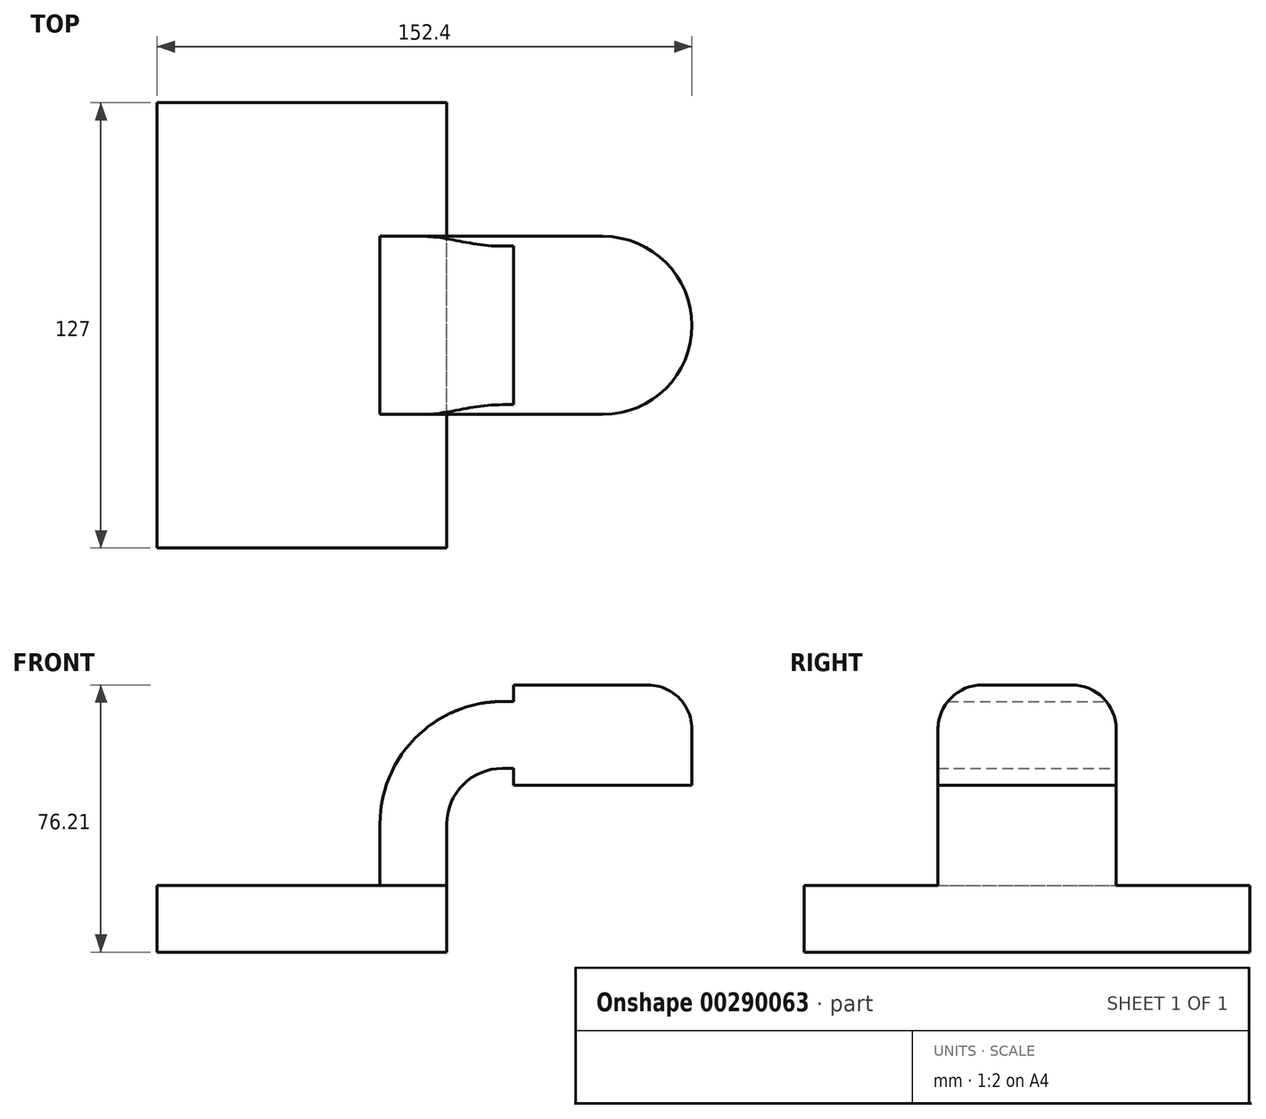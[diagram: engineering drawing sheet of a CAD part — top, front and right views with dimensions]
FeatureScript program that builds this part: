
annotation { "Feature Type Name" : "Feature", "Feature Type Description" : "" }
export const myFeature = defineFeature(function(context is Context, id is Id, definition is map)
    precondition{}
    {
        {
            var Q0;
            Q0=qCreatedBy(makeId("Front.planeOp"),FACE);
            var sketch = newSketch(context, id + "F0", { "sketchPlane" : qUnion([Q0])});
            skLineSegment(sketch, "E0.bottom", {"start": v(41.28, 9.53) * mm, "end": v(-41.28, 9.53) * mm});
            skLineSegment(sketch, "E0.top", {"start": v(41.28, -9.52) * mm, "end": v(-41.28, -9.52) * mm});
            skLineSegment(sketch, "E0.left", {"start": v(41.28, 9.53) * mm, "end": v(41.28, -9.52) * mm});
            skLineSegment(sketch, "E0.right", {"start": v(-41.28, 9.53) * mm, "end": v(-41.28, -9.53) * mm});
            skPoint(sketch, "E0.middle", {"position": v(0, 0) * mm});
            skLineSegment(sketch, "E1.bottom", {"start": v(111.13, 38.1) * mm, "end": v(60.33, 38.1) * mm});
            skLineSegment(sketch, "E1.top", {"start": v(111.13, 66.68) * mm, "end": v(60.33, 66.68) * mm});
            skLineSegment(sketch, "E1.left", {"start": v(111.13, 38.1) * mm, "end": v(111.13, 66.68) * mm});
            skLineSegment(sketch, "E1.right", {"start": v(60.33, 38.1) * mm, "end": v(60.33, 66.68) * mm});
            skPoint(sketch, "E1.middle", {"position": v(85.73, 52.39) * mm});
            skLineSegment(sketch, "E2", {"start": v(41.28, 9.53) * mm, "end": v(41.28, 27) * mm});
            skArc(sketch, "E3", {"start": v(41.28, 27) * mm, "mid": v(45.92, 38.23) * mm, "end": v(57.15, 42.88) * mm});
            skLineSegment(sketch, "E4", {"start": v(57.15, 42.88) * mm, "end": v(85.73, 42.88) * mm});
            skLineSegment(sketch, "E5.0", {"start": v(57.15, 61.93) * mm, "end": v(85.73, 61.93) * mm});
            skArc(sketch, "E5.1", {"start": v(22.23, 27) * mm, "mid": v(32.45, 51.7) * mm, "end": v(57.15, 61.93) * mm});
            skLineSegment(sketch, "E5.2", {"start": v(22.23, 9.53) * mm, "end": v(22.23, 27) * mm});
            skLineSegment(sketch, "E6", {"start": v(85.73, 38.1) * mm, "end": v(85.73, 66.68) * mm});
            skFitSpline(sketch, "E7", {"points": [v(-41.28, 9.53) * mm, v(57.15, 61.93) * mm], "startDerivative": vector(1.25, 131.22) * mm, "endDerivative": vector(147.95, -0.42) * mm});
            skSolve(sketch);
        }
        {
            var Q0;
            Q0=makeQuery(id+"F0.imprint","IMPRINT",FACE,{"disambiguationData":[TD([[makeQuery(id+"F0.imprint","IMPRINT",EDGE,{"derivedFrom":sQuery(id+"F0.wireOp",EDGE,"E0.top")}),-1.0]])]});
            extrude(context, id + "F1", {"entities" : qUnion([Q0]), "endBound" : BoundingType.SYMMETRIC, "depth" : 127 * mm});
        }
        {
            var Q0;
            {var subQ1=sQuery(id+"F0.wireOp",EDGE,"E2");Q0=makeQuery(id+"F0.imprint","IMPRINT",FACE,{"disambiguationData":[TD([[makeQuery(id+"F0.imprint","IMPRINT",EDGE,{"derivedFrom":subQ1}),1.0]])]});}
            var Q1;
            {var subQ0=sQuery(id+"F0.wireOp",EDGE,"E1.right");var subQ1=sQuery(id+"F0.wireOp",EDGE,"E1.bottom");var subQ2=makeQuery(id+"F0.imprint","INTERSECT",VERTEX,{"derivedFrom":[subQ1,subQ0]});Q1=makeQuery(id+"F0.imprint","IMPRINT",FACE,{"disambiguationData":[TD([[makeQuery(id+"F0.imprint","IMPRINT",EDGE,{"disambiguationData":[TD([[subQ2,1.0]])],"derivedFrom":subQ1}),-1.0]])]});}
            var Q2;
            {var subQ0=sQuery(id+"F0.wireOp",EDGE,"E4");var subQ1=sQuery(id+"F0.wireOp",EDGE,"E1.right");var subQ2=makeQuery(id+"F0.imprint","INTERSECT",VERTEX,{"derivedFrom":[subQ1,subQ0]});Q2=makeQuery(id+"F0.imprint","IMPRINT",FACE,{"disambiguationData":[TD([[makeQuery(id+"F0.imprint","IMPRINT",EDGE,{"disambiguationData":[TD([[subQ2,-1.0]])],"derivedFrom":subQ1}),-1.0]])]});}
            var Q3;
            {var subQ0=sQuery(id+"F0.wireOp",EDGE,"E1.right");var subQ1=sQuery(id+"F0.wireOp",EDGE,"E1.top");var subQ2=makeQuery(id+"F0.imprint","INTERSECT",VERTEX,{"derivedFrom":[subQ1,subQ0]});Q3=makeQuery(id+"F0.imprint","IMPRINT",FACE,{"disambiguationData":[TD([[makeQuery(id+"F0.imprint","IMPRINT",EDGE,{"disambiguationData":[TD([[subQ2,1.0]])],"derivedFrom":subQ1}),1.0]])]});}
            extrude(context, id + "F2", {"entities" : qUnion([Q0, Q1, Q2, Q3]), "operationType" : NewBodyOperationType.ADD, "endBound" : BoundingType.SYMMETRIC, "depth" : 50.8 * mm});
        }
        {
            var Q0;
            {var subQ4=sQuery(id+"F0.wireOp",EDGE,"E1.left");Q0=makeQuery(id+"F0.imprint","IMPRINT",FACE,{"disambiguationData":[TD([[makeQuery(id+"F0.imprint","IMPRINT",EDGE,{"derivedFrom":subQ4}),1.0]])]});}
            var Q1;
            Q1=sQuery(id+"F0.wireOp",EDGE,"E6");
            revolve(context, id + "F3", {"operationType" : NewBodyOperationType.ADD, "entities" : qUnion([Q0]), "axis" : qUnion([Q1]), "revolveType" : RevolveType.FULL});
        }
        {
            var Q0;
            Q0=makeQuery(id+"F0.imprint","IMPRINT",FACE,{"disambiguationData":[TD([[makeQuery(id+"F0.imprint","IMPRINT",EDGE,{"derivedFrom":sQuery(id+"F0.wireOp",EDGE,"E5.1")}),1.0]])]});
            extrude(context, id + "F4", {"entities" : qUnion([Q0]), "operationType" : NewBodyOperationType.ADD, "endBound" : BoundingType.SYMMETRIC, "depth" : 6.35 * mm});
        }
        {
            var Q0;
            Q0=makeQuery(id+"F3.opRevolve","SWEPT_EDGE",EDGE,{"disambiguationData":[OSD([sQuery(id+"F0.wireOp",EDGE,"E1.top"),sQuery(id+"F0.wireOp",EDGE,"E1.left")])]});
            fillet(context, id + "F5", {"entities" : qUnion([Q0]), "radius" : 12.7 * mm, "tangentPropagation" : true, "allowEdgeOverflow" : false});
        }
    });
